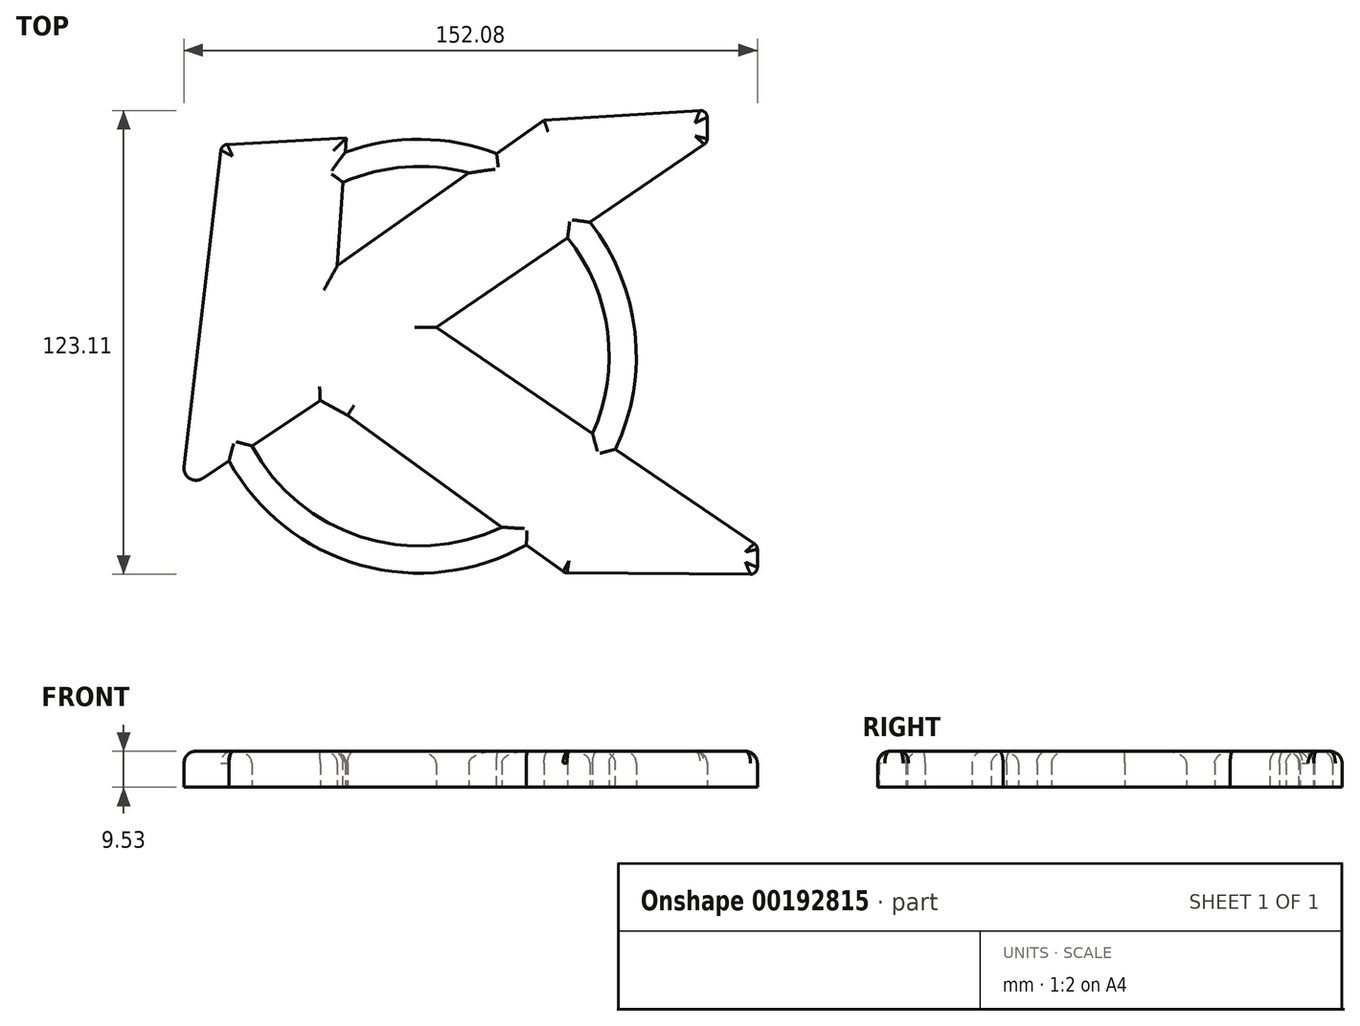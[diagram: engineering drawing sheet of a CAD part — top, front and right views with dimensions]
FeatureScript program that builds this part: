
annotation { "Feature Type Name" : "Feature", "Feature Type Description" : "" }
export const myFeature = defineFeature(function(context is Context, id is Id, definition is map)
    precondition{}
    {
        {
            var Q0;
            Q0=qCreatedBy(makeId("Top.planeOp"),FACE);
            var sketch = newSketch(context, id + "F0", { "sketchPlane" : qUnion([Q0])});
            skLineSegment(sketch, "E0", {"start": v(-40.56, -15.51) * mm, "end": v(-33.27, -19.43) * mm});
            skLineSegment(sketch, "E1", {"start": v(-33.27, -19.43) * mm, "end": v(7.61, -49.1) * mm});
            skArc(sketch, "E2", {"start": v(7.61, -49.1) * mm, "mid": v(-29.9, -51.65) * mm, "end": v(-58.73, -27.52) * mm});
            skLineSegment(sketch, "E3", {"start": v(-58.73, -27.52) * mm, "end": v(-40.56, -15.51) * mm});
            skArc(sketch, "E4", {"start": v(25.03, 27.74) * mm, "mid": v(35.67, 2.64) * mm, "end": v(31.68, -24.31) * mm});
            skLineSegment(sketch, "E5", {"start": v(31.68, -24.31) * mm, "end": v(-9.83, 3.9) * mm});
            skLineSegment(sketch, "E6", {"start": v(-9.83, 3.9) * mm, "end": v(25.03, 27.74) * mm});
            skArc(sketch, "E7", {"start": v(-34.5, 42.43) * mm, "mid": v(-18.01, 46.51) * mm, "end": v(-1.1, 44.89) * mm});
            skLineSegment(sketch, "E8", {"start": v(-1.1, 44.89) * mm, "end": v(-36, 20.28) * mm});
            skLineSegment(sketch, "E9", {"start": v(-36, 20.28) * mm, "end": v(-34.5, 42.43) * mm});
            skLineSegment(sketch, "E10", {"start": v(-33.7, 54.17) * mm, "end": v(-65.21, 52.5) * mm});
            skArc(sketch, "E11", {"start": v(-65.21, 52.5) * mm, "mid": v(-66.35, 52) * mm, "end": v(-66.9, 50.9) * mm});
            skLineSegment(sketch, "E12", {"start": v(-66.9, 50.9) * mm, "end": v(-77.47, -39.9) * mm});
            skLineSegment(sketch, "E13", {"start": v(-77.47, -39.9) * mm, "end": v(-64.76, -31.5) * mm});
            skArc(sketch, "E14", {"start": v(-64.76, -31.5) * mm, "mid": v(-29.99, -59.14) * mm, "end": v(14.1, -53.82) * mm});
            skLineSegment(sketch, "E15", {"start": v(14.1, -53.82) * mm, "end": v(23.86, -60.9) * mm});
            skArc(sketch, "E16", {"start": v(23.86, -60.9) * mm, "mid": v(24.36, -61.15) * mm, "end": v(24.9, -61.24) * mm});
            skLineSegment(sketch, "E17", {"start": v(24.9, -61.24) * mm, "end": v(73.57, -61.61) * mm});
            skArc(sketch, "E18", {"start": v(73.57, -61.61) * mm, "mid": v(74.85, -61.09) * mm, "end": v(75.38, -59.81) * mm});
            skLineSegment(sketch, "E19", {"start": v(75.38, -59.81) * mm, "end": v(75.38, -54.97) * mm});
            skArc(sketch, "E20", {"start": v(75.38, -54.97) * mm, "mid": v(75.17, -54.13) * mm, "end": v(74.6, -53.48) * mm});
            skLineSegment(sketch, "E21", {"start": v(74.6, -53.48) * mm, "end": v(37.71, -28.42) * mm});
            skArc(sketch, "E22", {"start": v(37.71, -28.42) * mm, "mid": v(42.91, 2.65) * mm, "end": v(31, 31.8) * mm});
            skLineSegment(sketch, "E23", {"start": v(31, 31.8) * mm, "end": v(61.29, 52.51) * mm});
            skArc(sketch, "E24", {"start": v(61.29, 52.51) * mm, "mid": v(61.86, 53.16) * mm, "end": v(62.07, 54) * mm});
            skLineSegment(sketch, "E25", {"start": v(62.07, 54) * mm, "end": v(62.07, 59.7) * mm});
            skArc(sketch, "E26", {"start": v(62.07, 59.7) * mm, "mid": v(61.5, 61) * mm, "end": v(60.16, 61.5) * mm});
            skLineSegment(sketch, "E27", {"start": v(60.16, 61.5) * mm, "end": v(18.8, 58.93) * mm});
            skLineSegment(sketch, "E28", {"start": v(18.8, 58.93) * mm, "end": v(6.22, 50.06) * mm});
            skArc(sketch, "E29", {"start": v(6.22, 50.06) * mm, "mid": v(-13.83, 53.84) * mm, "end": v(-33.95, 50.4) * mm});
            skLineSegment(sketch, "E30", {"start": v(-33.95, 50.4) * mm, "end": v(-33.7, 54.17) * mm});
            skPoint(sketch, "E31.orphan", {"position": v(-77.02, -36.06) * mm});
            skSolve(sketch);
        }
        {
            var Q0;
            Q0=makeQuery(id+"F0.imprint","IMPRINT",FACE,{"disambiguationData":[TD([[makeQuery(id+"F0.imprint","IMPRINT",EDGE,{"derivedFrom":sQuery(id+"F0.wireOp",EDGE,"E0")}),1.0]])]});
            extrude(context, id + "F1", {"entities" : qUnion([Q0]), "depth" : 9.52 * mm});
        }
        {
            var Q0;
            Q0=makeQuery(id+"F1.opExtrude","CAP_FACE",FACE,{"disambiguationData":[OSD([sQuery(id+"F0.wireOp",EDGE,"E0"),sQuery(id+"F0.wireOp",EDGE,"E1"),sQuery(id+"F0.wireOp",EDGE,"E2"),sQuery(id+"F0.wireOp",EDGE,"E3"),sQuery(id+"F0.wireOp",EDGE,"E4"),sQuery(id+"F0.wireOp",EDGE,"E5"),sQuery(id+"F0.wireOp",EDGE,"E6"),sQuery(id+"F0.wireOp",EDGE,"E7"),sQuery(id+"F0.wireOp",EDGE,"E8"),sQuery(id+"F0.wireOp",EDGE,"E9"),sQuery(id+"F0.wireOp",EDGE,"E10"),sQuery(id+"F0.wireOp",EDGE,"E11"),sQuery(id+"F0.wireOp",EDGE,"E12"),sQuery(id+"F0.wireOp",EDGE,"E13"),sQuery(id+"F0.wireOp",EDGE,"E14"),sQuery(id+"F0.wireOp",EDGE,"E15"),sQuery(id+"F0.wireOp",EDGE,"E16"),sQuery(id+"F0.wireOp",EDGE,"E17"),sQuery(id+"F0.wireOp",EDGE,"E18"),sQuery(id+"F0.wireOp",EDGE,"E19"),sQuery(id+"F0.wireOp",EDGE,"E20"),sQuery(id+"F0.wireOp",EDGE,"E21"),sQuery(id+"F0.wireOp",EDGE,"E22"),sQuery(id+"F0.wireOp",EDGE,"E23"),sQuery(id+"F0.wireOp",EDGE,"E24"),sQuery(id+"F0.wireOp",EDGE,"E25"),sQuery(id+"F0.wireOp",EDGE,"E26"),sQuery(id+"F0.wireOp",EDGE,"E27"),sQuery(id+"F0.wireOp",EDGE,"E28"),sQuery(id+"F0.wireOp",EDGE,"E29"),sQuery(id+"F0.wireOp",EDGE,"E30")])],"isStart":false});
            fillet(context, id + "F2", {"entities" : qUnion([Q0]), "radius" : 3.17 * mm, "tangentPropagation" : true, "allowEdgeOverflow" : false});
        }
        {
            var Q0;
            Q0=makeQuery(id+"F1.opExtrude","SWEPT_EDGE",EDGE,{"disambiguationData":[OSD([sQuery(id+"F0.wireOp",EDGE,"E12"),sQuery(id+"F0.wireOp",EDGE,"E13")])]});
            fillet(context, id + "F3", {"entities" : qUnion([Q0]), "radius" : 3.17 * mm, "tangentPropagation" : true, "allowEdgeOverflow" : false});
        }
    });
